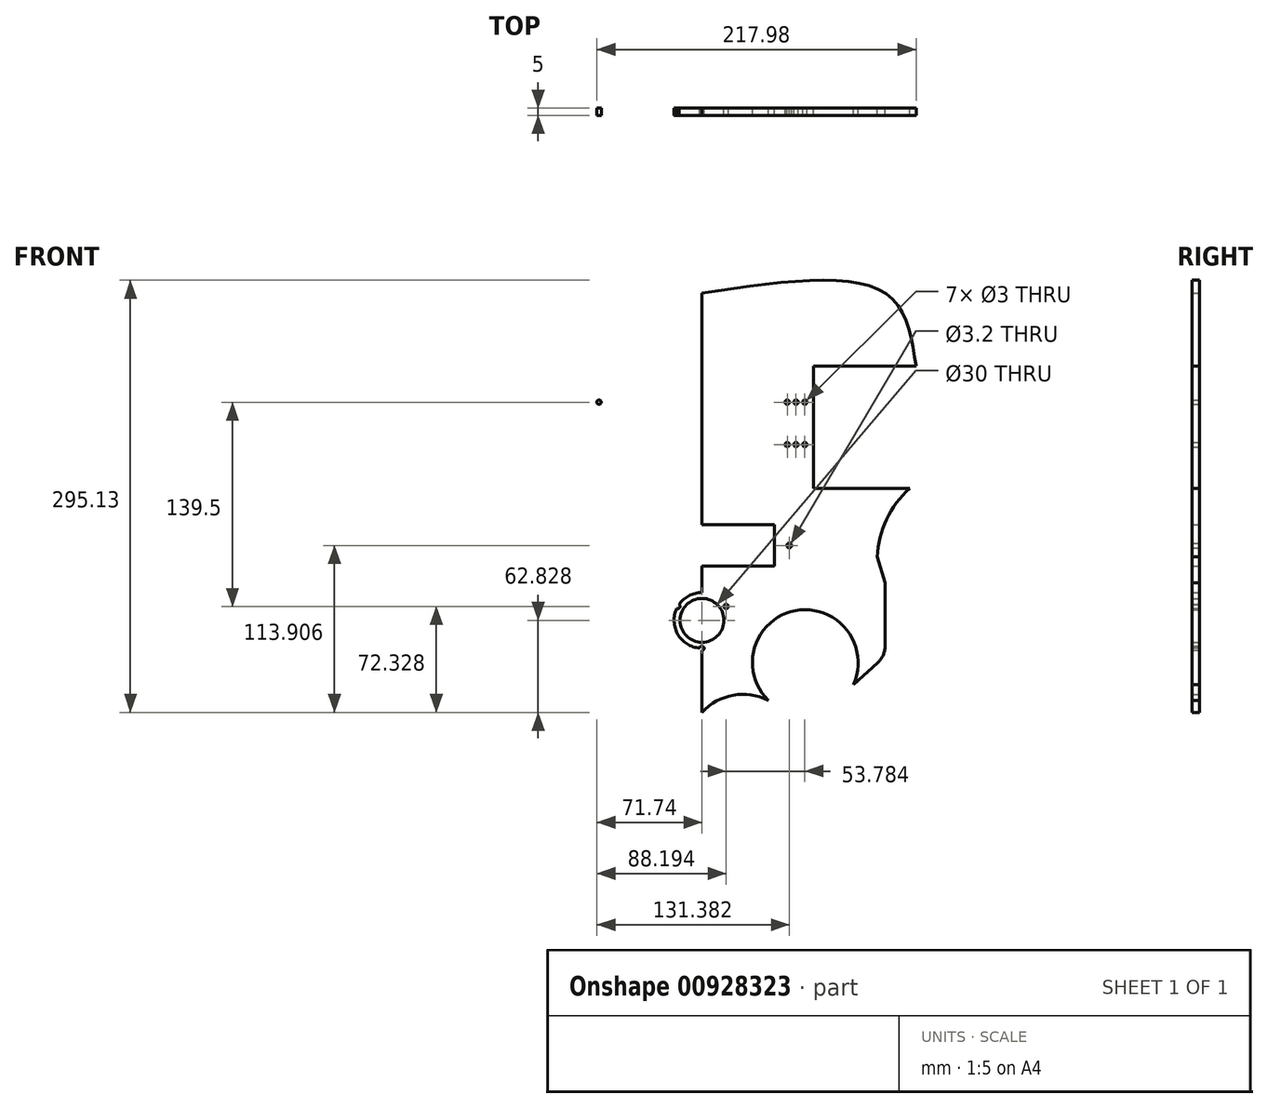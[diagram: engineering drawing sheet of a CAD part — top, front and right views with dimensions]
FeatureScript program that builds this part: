
annotation { "Feature Type Name" : "Feature", "Feature Type Description" : "" }
export const myFeature = defineFeature(function(context is Context, id is Id, definition is map)
    precondition{}
    {
        {
            var Q0;
            Q0=qCreatedBy(makeId("Front.planeOp"),FACE);
            var sketch = newSketch(context, id + "F0", { "sketchPlane" : qUnion([Q0])});
            skPoint(sketch, "E0.middle", {"position": v(0, 0) * mm});
            skLineSegment(sketch, "E1", {"start": v(0, -98.93) * mm, "end": v(0, -87.64) * mm});
            skLineSegment(sketch, "E2", {"start": v(-125, 48.93) * mm, "end": v(-76.24, 48.93) * mm});
            skLineSegment(sketch, "E3.MirrorCS", {"start": v(125, 48.93) * mm, "end": v(76.24, 48.93) * mm});
            skCircle(sketch, "E4", {"center": v(-70.24, 24.43) * mm, "radius": 1.5 * mm});
            skCircle(sketch, "E5", {"center": v(-58.24, 24.43) * mm, "radius": 1.5 * mm});
            skCircle(sketch, "E6", {"center": v(-64.24, 24.43) * mm, "radius": 1.5 * mm});
            skCircle(sketch, "E7", {"center": v(-70.24, -4.57) * mm, "radius": 1.5 * mm});
            skCircle(sketch, "E8", {"center": v(-58.24, -4.57) * mm, "radius": 1.5 * mm});
            skCircle(sketch, "E9", {"center": v(-64.19, -4.57) * mm, "radius": 1.5 * mm});
            skCircle(sketch, "E10.MirrorC", {"center": v(70.24, 24.43) * mm, "radius": 1.5 * mm});
            skCircle(sketch, "E11.MirrorC", {"center": v(64.24, 24.43) * mm, "radius": 1.5 * mm});
            skCircle(sketch, "E12.MirrorC", {"center": v(58.24, 24.43) * mm, "radius": 1.5 * mm});
            skCircle(sketch, "E13.MirrorC", {"center": v(58.24, -4.57) * mm, "radius": 1.5 * mm});
            skCircle(sketch, "E14.MirrorC", {"center": v(64.19, -4.57) * mm, "radius": 1.5 * mm});
            skCircle(sketch, "E15.MirrorC", {"center": v(70.24, -4.57) * mm, "radius": 1.5 * mm});
            skLineSegment(sketch, "E16.0", {"start": v(-49.5, -59.35) * mm, "end": v(49.5, -59.35) * mm});
            skLineSegment(sketch, "E16.3", {"start": v(49.5, -87.64) * mm, "end": v(-49.5, -87.64) * mm});
            skPoint(sketch, "E16.0.midPoint", {"position": v(0, -59.35) * mm});
            skCircle(sketch, "E17", {"center": v(0, -124.57) * mm, "radius": 15 * mm});
            skLineSegment(sketch, "E18", {"start": v(-125, -98.93) * mm, "end": v(-125, -142.24) * mm});
            skLineSegment(sketch, "E19", {"start": v(125, -142.24) * mm, "end": v(125, -98.93) * mm});
            skCircle(sketch, "E20", {"center": v(-59.64, -73.5) * mm, "radius": 1.6 * mm});
            skLineSegment(sketch, "E21", {"start": v(-49.5, -59.35) * mm, "end": v(-49.5, -87.64) * mm});
            skCircle(sketch, "E22.MirrorC", {"center": v(59.64, -73.5) * mm, "radius": 1.6 * mm});
            skLineSegment(sketch, "E23.MirrorCS", {"start": v(49.5, -59.35) * mm, "end": v(49.5, -87.64) * mm});
            skPoint(sketch, "E16.4.end.orphan", {"position": v(-63.64, -73.5) * mm});
            skPoint(sketch, "E24.visualSharp", {"position": v(-125, -148.93) * mm});
            skArc(sketch, "E24.filletArc", {"start": v(-125, -142.24) * mm, "mid": v(-123.7, -148.35) * mm, "end": v(-120.02, -153.4) * mm});
            skPoint(sketch, "E25.visualSharp", {"position": v(125, -148.93) * mm});
            skArc(sketch, "E25.filletArc", {"start": v(120.02, -153.4) * mm, "mid": v(123.7, -148.35) * mm, "end": v(125, -142.24) * mm});
            skPoint(sketch, "E26.MirrorCS.end.orphan", {"position": v(125, 48.93) * mm});
            skPoint(sketch, "E26.MirrorCS.start.orphan", {"position": v(125, 98.93) * mm});
            skLineSegment(sketch, "E27", {"start": v(119.72, -81.3) * mm, "end": v(125, -98.93) * mm});
            skLineSegment(sketch, "E28", {"start": v(-119.72, -81.3) * mm, "end": v(-125, -98.93) * mm});
            skArc(sketch, "E29", {"start": v(141.9, -34.57) * mm, "mid": v(125.99, -55.65) * mm, "end": v(119.72, -81.3) * mm});
            skLineSegment(sketch, "E30", {"start": v(146.24, 48.93) * mm, "end": v(125, 48.93) * mm});
            skFitSpline(sketch, "E31", {"points": [v(146.24, 48.93) * mm, v(125, 98.93) * mm, v(0, 98.93) * mm], "startDerivative": vector(-22.87, 150.85) * mm, "endDerivative": vector(-253.8, -37.92) * mm});
            skPoint(sketch, "E32.start.orphan", {"position": v(-125, 98.93) * mm});
            skPoint(sketch, "E33.end.orphan", {"position": v(-104.67, -31.07) * mm});
            skArc(sketch, "E34.MirrorCS", {"start": v(-141.9, -34.57) * mm, "mid": v(-125.99, -55.65) * mm, "end": v(-119.72, -81.3) * mm});
            skLineSegment(sketch, "E35.MirrorCS", {"start": v(-146.24, 48.93) * mm, "end": v(-125, 48.93) * mm});
            skFitSpline(sketch, "E36.MirrorCS", {"points": [v(-146.24, 48.93) * mm, v(-125, 98.93) * mm, v(0, 98.93) * mm], "startDerivative": vector(22.87, 150.85) * mm, "endDerivative": vector(253.8, -37.92) * mm});
            skLineSegment(sketch, "E37.trimOffspring", {"start": v(0, -59.35) * mm, "end": v(0, 98.93) * mm});
            skPoint(sketch, "E38.MirrorCS.end.orphan", {"position": v(104.67, -31.07) * mm});
            skPoint(sketch, "E39.orphan", {"position": v(76.24, -31.07) * mm});
            skPoint(sketch, "E40.orphan", {"position": v(-76.24, -31.07) * mm});
            skPoint(sketch, "E41.MirrorCS.start.orphan", {"position": v(-146.24, -31.07) * mm});
            skLineSegment(sketch, "E42", {"start": v(-70.24, -4.57) * mm, "end": v(-70.24, -34.57) * mm});
            skLineSegment(sketch, "E43", {"start": v(-76.24, 48.93) * mm, "end": v(-76.24, -34.57) * mm});
            skLineSegment(sketch, "E44", {"start": v(-76.24, -34.57) * mm, "end": v(-141.9, -34.57) * mm});
            skLineSegment(sketch, "E45.MirrorCS", {"start": v(76.24, -34.57) * mm, "end": v(141.9, -34.57) * mm});
            skPoint(sketch, "E46.orphan", {"position": v(146.24, -31.07) * mm});
            skPoint(sketch, "E47.MirrorCS.start.orphan", {"position": v(76.24, 48.93) * mm});
            skLineSegment(sketch, "E48.MirrorCS", {"start": v(76.24, 48.93) * mm, "end": v(76.24, -34.57) * mm});
            skLineSegment(sketch, "E49", {"start": v(-120.02, -153.4) * mm, "end": v(-103.43, -168.3) * mm});
            skLineSegment(sketch, "E50", {"start": v(0, 98.93) * mm, "end": v(0, -139.57) * mm});
            skArc(sketch, "E51", {"start": v(-45.33, -179.22) * mm, "mid": v(-63.89, -117.93) * mm, "end": v(-103.43, -168.3) * mm});
            skArc(sketch, "E52.MirrorCS", {"start": v(45.33, -179.22) * mm, "mid": v(63.89, -117.93) * mm, "end": v(103.43, -168.3) * mm});
            skLineSegment(sketch, "E53.MirrorCS", {"start": v(120.02, -153.4) * mm, "end": v(103.43, -168.3) * mm});
            skPoint(sketch, "E54.MirrorCS.end.orphan", {"position": v(45.33, -179.22) * mm});
            skPoint(sketch, "E54.MirrorCS.start.orphan", {"position": v(0, -171.83) * mm});
            skArc(sketch, "E55", {"start": v(-43.22, -176.98) * mm, "mid": v(-44.3, -178.07) * mm, "end": v(-45.33, -179.22) * mm});
            skArc(sketch, "E56.MirrorCS", {"start": v(43.22, -176.98) * mm, "mid": v(44.3, -178.07) * mm, "end": v(45.33, -179.22) * mm});
            skLineSegment(sketch, "E57", {"start": v(0, -139.57) * mm, "end": v(0, -179.22) * mm});
            skLineSegment(sketch, "E58", {"start": v(0, -179.22) * mm, "end": v(0, -187.4) * mm});
            skArc(sketch, "E59", {"start": v(0, -187.4) * mm, "mid": v(-21.28, -175.64) * mm, "end": v(-45.33, -179.22) * mm});
            skArc(sketch, "E60.MirrorCS", {"start": v(0, -187.4) * mm, "mid": v(21.28, -175.64) * mm, "end": v(45.33, -179.22) * mm});
            skCircle(sketch, "E61", {"center": v(-275.8, 31.72) * mm, "radius": 26.79 * mm});
            skEllipse(sketch, "E62", {"center": v(-275.8, 31.72) * mm, "majorRadius": 26.26 * mm, "minorRadius": 24 * mm, "majorAxis": v(1, 0)});
            skLineSegment(sketch, "E63.bottom", {"start": v(-309.33, 11.72) * mm, "end": v(-236.46, 11.72) * mm});
            skLineSegment(sketch, "E63.top", {"start": v(-309.33, 51.72) * mm, "end": v(-236.46, 51.72) * mm});
            skLineSegment(sketch, "E63.right", {"start": v(-236.46, 11.72) * mm, "end": v(-236.46, 51.72) * mm});
            skLineSegment(sketch, "E64.bottom", {"start": v(-258.45, 71.05) * mm, "end": v(-293.14, 71.05) * mm});
            skLineSegment(sketch, "E64.top", {"start": v(-258.45, -7.62) * mm, "end": v(-293.14, -7.62) * mm});
            skLineSegment(sketch, "E64.left", {"start": v(-258.45, 71.05) * mm, "end": v(-258.45, -7.62) * mm});
            skLineSegment(sketch, "E64.right", {"start": v(-293.14, 71.05) * mm, "end": v(-293.14, -7.62) * mm});
            skCircle(sketch, "E65.cCircle", {"center": v(-275.8, 31.72) * mm, "radius": 39.05 * mm, "construction": true});
            skLineSegment(sketch, "E65.0", {"start": v(-242.26, 51.72) * mm, "end": v(-241.7, 12.67) * mm});
            skLineSegment(sketch, "E65.1", {"start": v(-241.7, 12.67) * mm, "end": v(-275.24, -7.33) * mm});
            skLineSegment(sketch, "E65.2", {"start": v(-275.24, -7.33) * mm, "end": v(-293.14, 2.67) * mm});
            skLineSegment(sketch, "E65.4", {"start": v(-309.88, 50.76) * mm, "end": v(-276.35, 70.76) * mm});
            skLineSegment(sketch, "E65.5", {"start": v(-276.35, 70.76) * mm, "end": v(-242.26, 51.72) * mm});
            skLineSegment(sketch, "E66.bottom", {"start": v(-293.14, -7.62) * mm, "end": v(-258.19, -7.62) * mm});
            skPoint(sketch, "E67.orphan", {"position": v(-315.13, 51.72) * mm});
            skPoint(sketch, "E68.orphan", {"position": v(-315.13, 11.72) * mm});
            skLineSegment(sketch, "E69", {"start": v(-276.35, 70.76) * mm, "end": v(-341.82, 31.72) * mm});
            skLineSegment(sketch, "E70", {"start": v(-275.24, -7.33) * mm, "end": v(-341.82, 31.72) * mm});
            skCircle(sketch, "E71", {"center": v(0, -124.57) * mm, "radius": 19 * mm});
            skCircle(sketch, "E72", {"center": v(0, -143.57) * mm, "radius": 1.5 * mm});
            skCircle(sketch, "E73.1.0", {"center": v(16.45, -115.07) * mm, "radius": 1.5 * mm});
            skCircle(sketch, "E73.2.0", {"center": v(-16.45, -115.07) * mm, "radius": 1.5 * mm});
            skSolve(sketch);
        }
        {
            var Q0;
            Q0=makeQuery(id+"F0.imprint","IMPRINT",FACE,{"disambiguationData":[TD([[makeQuery(id+"F0.imprint","IMPRINT",EDGE,{"derivedFrom":sQuery(id+"F0.wireOp",EDGE,"E3.MirrorCS")}),-1.0]])]});
            var Q1;
            Q1=makeQuery(id+"F0.imprint","IMPRINT",FACE,{"disambiguationData":[TD([[makeQuery(id+"F0.imprint","IMPRINT",EDGE,{"derivedFrom":sQuery(id+"F0.wireOp",EDGE,"E4")}),1.0]])]});
            var Q2;
            {var subQ1=sQuery(id+"F0.wireOp",EDGE,"E50");var subQ2=sQuery(id+"F0.wireOp",EDGE,"E17");var subQ11=makeQuery(id+"F0.imprint","INTERSECT",VERTEX,{"derivedFrom":[subQ2,subQ1]});Q2=makeQuery(id+"F0.imprint","IMPRINT",FACE,{"disambiguationData":[TD([[makeQuery(id+"F0.imprint","IMPRINT",EDGE,{"disambiguationData":[TD([[subQ11,1.0]])],"derivedFrom":subQ1}),-1.0]])]});}
            var Q3;
            {var subQ1=sQuery(id+"F0.wireOp",EDGE,"E50");var subQ7=sQuery(id+"F0.wireOp",EDGE,"E17");var subQ11=makeQuery(id+"F0.imprint","INTERSECT",VERTEX,{"derivedFrom":[subQ7,subQ1]});Q3=makeQuery(id+"F0.imprint","IMPRINT",FACE,{"disambiguationData":[TD([[makeQuery(id+"F0.imprint","IMPRINT",EDGE,{"disambiguationData":[TD([[subQ11,1.0]])],"derivedFrom":subQ1}),1.0]])]});}
            extrude(context, id + "F1", {"entities" : qUnion([Q0, Q1, Q2, Q3]), "depth" : 5 * mm, "offsetDistance" : 25 * mm});
        }
    });
